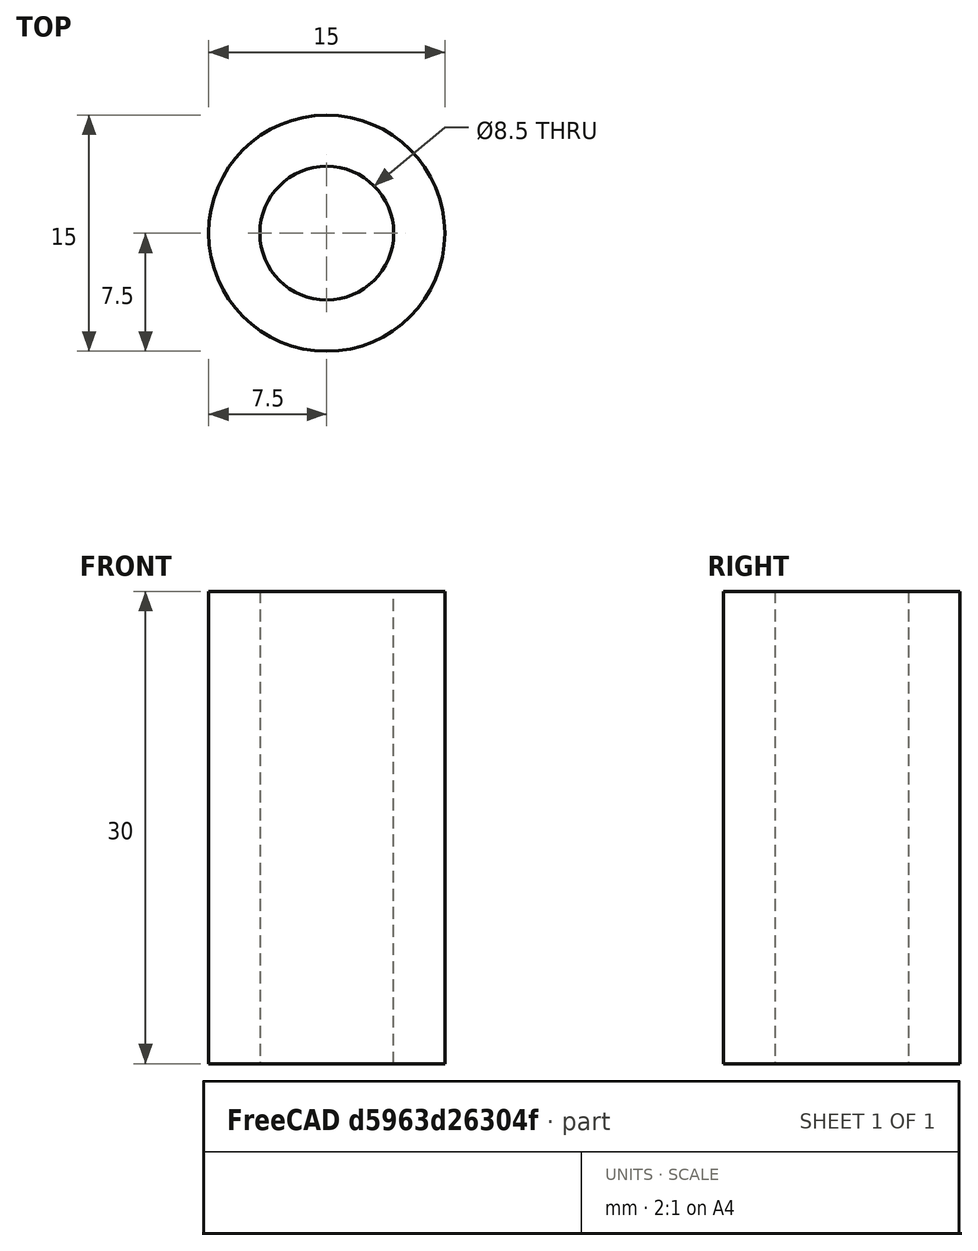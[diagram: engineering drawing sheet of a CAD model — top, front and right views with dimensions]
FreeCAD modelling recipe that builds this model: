
FCSTD DOCUMENT  (FreeCAD 0.21R33694 (Git))
Label: cable_sleeve
License: All rights reserved
LicenseURL: http://en.wikipedia.org/wiki/All_rights_reserved
objects: Spreadsheet::Sheet×1, Sketcher::SketchObject×1, PartDesign::Pad×1, PartDesign::Body×1
note: 4 computed .brp shape members not serialized (recipe doc carries the construction recipe); baked Part::Feature solids carry a one-line shape summary decoded from their .brp

FEATURE [Spreadsheet::Sheet] Spreadsheet  label="settings"
  cells = A1='Outer diameter; B1(dia_outer)=15; A2='inner diameter; B2(dia_inner)=8.5; A3='Height; B3(height)=30
FEATURE [Sketcher::SketchObject] Sketch
  FullyConstrained = true
  MapMode = 5
  Support = -> [XY_Plane]
  expr: Constraints[2] = <<settings>>.dia_inner
  expr: Constraints[3] = <<settings>>.dia_outer
  sketch-geometry (2):
    g0: Circle CenterX=0 CenterY=0 CenterZ=0 NormalX=0 NormalY=0 NormalZ=1 AngleXU=0 Radius=4.25
    g1: Circle CenterX=0 CenterY=0 CenterZ=0 NormalX=0 NormalY=0 NormalZ=1 AngleXU=0 Radius=7.5
  constraints (4):
    c: Coincident(g0,g-1)
    c: Coincident(g1,g0)
    c: Diameter(g0) = 8.5
    c: Diameter(g1) = 15
FEATURE [PartDesign::Pad] Pad  label="main_body"
  Direction = (0,0,1)
  Length = 30
  Length2 = 10
  Profile = -> Sketch
  ReferenceAxis = -> Sketch [N_Axis]
  Type = 0
  expr: Length = <<settings>>.height
FEATURE [PartDesign::Body] Body
  Group = -> [Sketch,Pad]
  Origin = -> Origin
  Tip = -> Pad
